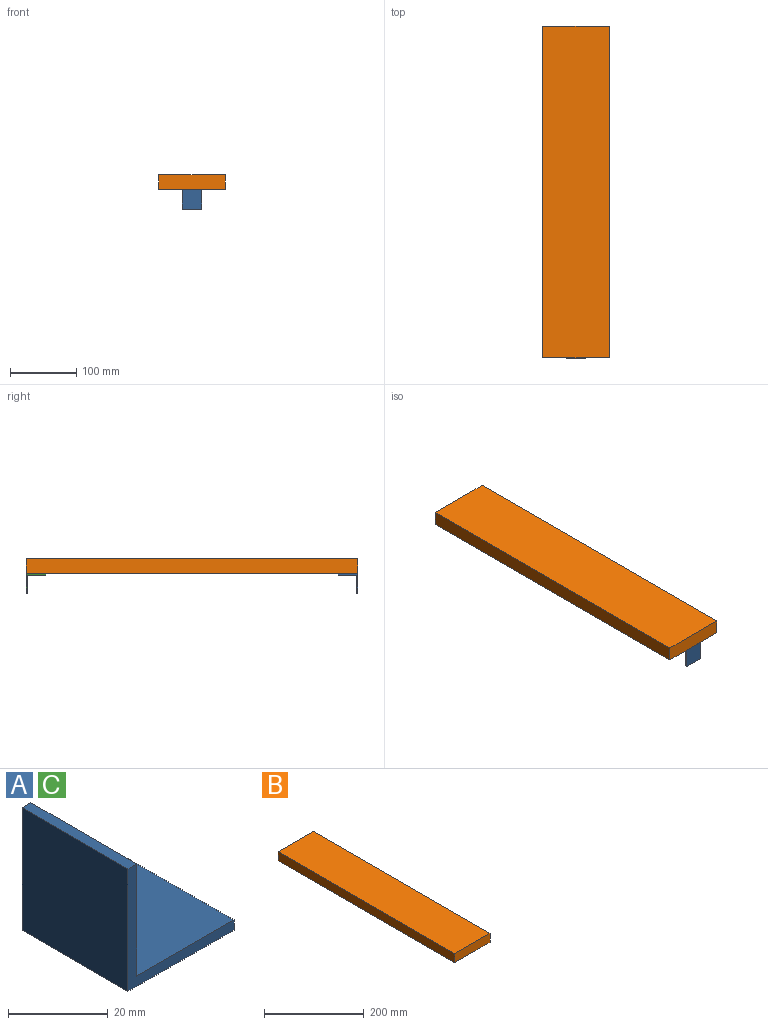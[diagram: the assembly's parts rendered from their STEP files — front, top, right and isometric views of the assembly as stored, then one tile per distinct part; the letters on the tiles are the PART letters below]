
ASSEMBLY  parts=3 mates=2
PART A: 8 faces, bbox 30x30x30 mm
  f0: plane 30x27.5mm, normal (0,0,1), area 825mm2, adj f1,f5,f6,f7
  f1: plane 30x27.5mm, normal (1,0,0), area 825mm2, adj f0,f2,f6,f7
  f2: plane 30x2.5mm, normal (0,0,1), area 75mm2, adj f1,f3,f6,f7
  f3: plane 30x30mm, normal (-1,0,0), area 900mm2, adj f2,f4,f6,f7
  f4: plane 30x30mm, normal (0,0,-1), area 900mm2, adj f3,f5,f6,f7
  f5: plane 30x2.5mm, normal (1,0,0), area 75mm2, adj f0,f4,f6,f7
  f6: plane 30x30mm, normal (0,-1,0), area 143.8mm2, adj f0,f1,f2,f3,f4,f5
  f7: plane 30x30mm, normal (0,1,0), area 143.8mm2, adj f0,f1,f2,f3,f4,f5
PART B: 6 faces, bbox 100x500x22 mm
  f0: plane 500x100mm, normal (0,0,-1), area 50000mm2, adj f1,f3,f4,f5
  f1: plane 500x22mm, normal (1,0,0), area 11000mm2, adj f0,f2,f4,f5
  f2: plane 500x100mm, normal (0,0,1), area 50000mm2, adj f1,f3,f4,f5
  f3: plane 500x22mm, normal (-1,0,0), area 11000mm2, adj f0,f2,f4,f5
  f4: plane 100x22mm, normal (0,-1,0), area 2200mm2, adj f0,f1,f2,f3
  f5: plane 100x22mm, normal (0,1,0), area 2200mm2, adj f0,f1,f2,f3
PART C: same geometry as A
PLACE A rot(axis=(-0.58,0.58,0.58),120deg) t=(-262.55,-449.14,-101.59)mm
PLACE B t=(-247.55,48.36,-88.09)mm
PLACE C rot(axis=(-0.71,0.71,0),180deg) t=(-262.55,45.86,-101.59)mm
MATE fastened C.f4 <-> B.f0  axis (0,0,1) through (-247.55,48.36,-99.09)mm
MATE fastened A.f3 <-> B.f0  axis (0,0,1) through (-247.55,-451.64,-99.09)mm
